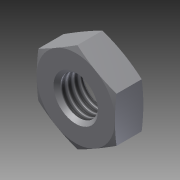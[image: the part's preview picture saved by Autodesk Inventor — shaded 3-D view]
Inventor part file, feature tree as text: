
AUTODESK INVENTOR PART (.ipt)
format: ipt  version: 2012 (Build 160160000, 160)  size: 146,432 bytes
history: native  units: in
note: dims shown in document units (in); Inventor stores cm internally (conversion verified against a paired STEP export)
features: other x70, sketch x3, revolve x2, extrude x1, thread x1
ambient origin geometry x8: Origin, YZ Plane, XZ Plane, XY Plane, X Axis, Y Axis, Z Axis, Center Point
bodies: Solid1 (feature_tree)
feature tree (77):
  sketch  "Sketch_8"  dims[d0=360.0deg d1=0.16in d2=0.0in]
  sketch  "Sketch_10"  dims[d3=360.0deg d4=0.1213in d5=0.0in]
  revolve  "Revolution1"  [1 undecoded]
  extrude  "Extrusion1"  Depth=0.1213in TaperAngle=0.0deg
  revolve  "Revolution2"  [1 undecoded]
  thread  "Thread1"  [1 undecoded]
  other  "NUT_XY"
  other  "NUT_YZ"
  other  "NUT_ZX"
  other  "NUT_X"
  other  "NUT_Y"
  other  "NUT_Z"
  other  "NUT_Center"
  other  "a1_XY"
  other  "a1_YZ"
  other  "a1_ZX"
  other  "a1_X"
  other  "a1_Y"
  other  "a1_Z"
  other  "a1_Center"
  other  "a2_XY"
  other  "a2_YZ"
  other  "a2_ZX"
  other  "a2_X"
  other  "a2_Y"
  other  "a2_Z"
  other  "a2_Center"
  other  "b1_XY"
  other  "b1_YZ"
  other  "b1_ZX"
  other  "b1_X"
  other  "b1_Y"
  other  "b1_Z"
  other  "b1_Center"
  other  "b2_XY"
  other  "b2_YZ"
  other  "b2_ZX"
  other  "b2_X"
  other  "b2_Y"
  other  "b2_Z"
  other  "b2_Center"
  other  "e_XY"
  other  "e_YZ"
  other  "e_ZX"
  other  "e_X"
  other  "e_Y"
  other  "e_Z"
  other  "e_Center"
  other  "th1_XY"
  other  "th1_YZ"
  other  "th1_ZX"
  other  "th1_X"
  other  "th1_Y"
  other  "th1_Z"
  other  "th1_Center"
  other  "th2_XY"
  other  "th2_YZ"
  other  "th2_ZX"
  other  "th2_X"
  other  "th2_Y"
  other  "th2_Z"
  other  "th2_Center"
  other  "ol1_XY"
  other  "ol1_YZ"
  other  "ol1_ZX"
  other  "ol1_X"
  other  "ol1_Y"
  other  "ol1_Z"
  other  "ol1_Center"
  other  "ol2_XY"
  other  "ol2_YZ"
  other  "ol2_ZX"
  other  "ol2_X"
  other  "ol2_Y"
  other  "ol2_Z"
  other  "ol2_Center"
  sketch  "Sketch_11"
note: 3 required parameter values undecoded (feature->parameter linkage not recoverable at this tier; creation-order binding heuristic only, values carry confidence <= 0.55)